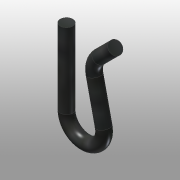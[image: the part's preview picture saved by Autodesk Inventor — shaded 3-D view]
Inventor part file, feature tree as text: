
AUTODESK INVENTOR PART (.ipt)
format: ipt  version: 2016 (Build 200138000, 138)  size: 124,928 bytes
history: native  units: mm
features: sketch x2, sweep x1
ambient origin geometry x8: Origin, YZ Plane, XZ Plane, XY Plane, X Axis, Y Axis, Z Axis, Center Point
bodies: Solid1 (feature_tree)
feature tree (3):
  sweep  "Sweep1"
  sketch  "Sketch1"  dims[d0=2.0mm d1=1.0mm]
  sketch  "Sketch2"  dims[d2=6.0mm d3=1.78mm d4=3.9mm d5=2.2mm d6=45.0deg d8=1.0mm d9=0.5mm d10=0.0mm d11=0.0mm]
